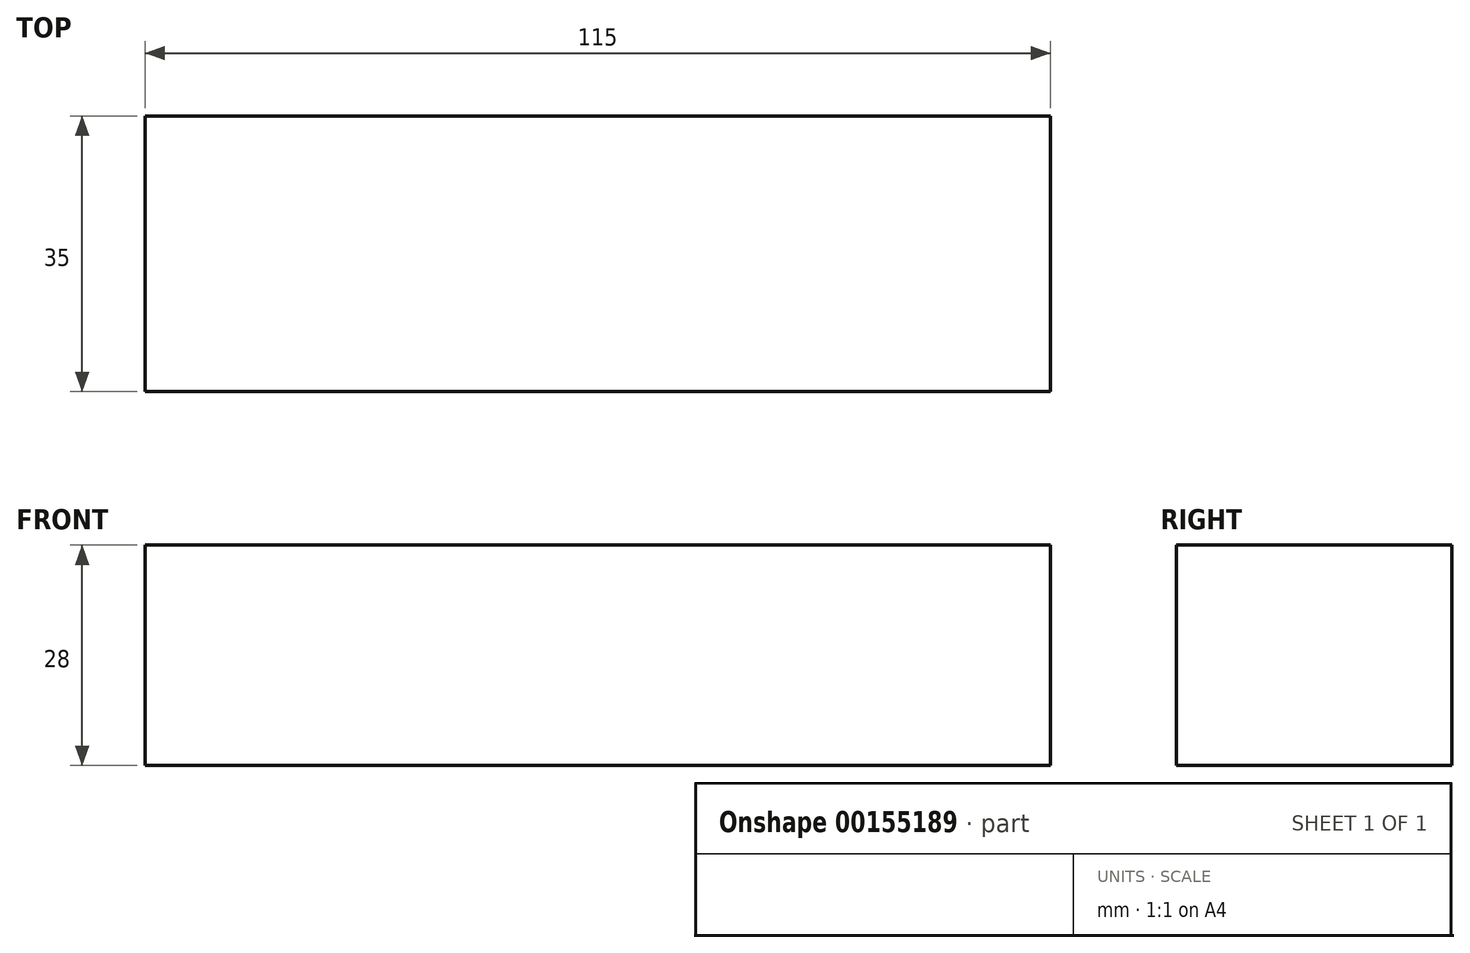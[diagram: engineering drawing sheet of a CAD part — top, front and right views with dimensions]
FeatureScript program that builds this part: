
annotation { "Feature Type Name" : "Feature", "Feature Type Description" : "" }
export const myFeature = defineFeature(function(context is Context, id is Id, definition is map)
    precondition{}
    {
        {
            var Q0;
            Q0=qCreatedBy(makeId("Top.planeOp"),FACE);
            var sketch = newSketch(context, id + "F0", { "sketchPlane" : qUnion([Q0])});
            skLineSegment(sketch, "E0.bottom", {"start": v(57.5, 17.5) * mm, "end": v(-57.5, 17.5) * mm});
            skLineSegment(sketch, "E0.top", {"start": v(57.5, -17.5) * mm, "end": v(-57.5, -17.5) * mm});
            skLineSegment(sketch, "E0.left", {"start": v(57.5, 17.5) * mm, "end": v(57.5, -17.5) * mm});
            skLineSegment(sketch, "E0.right", {"start": v(-57.5, 17.5) * mm, "end": v(-57.5, -17.5) * mm});
            skPoint(sketch, "E0.middle", {"position": v(0, 0) * mm});
            skSolve(sketch);
        }
        {
            var Q0;
            Q0=qSketchRegion(id+"F0",true);
            extrude(context, id + "F1", {"entities" : qUnion([Q0]), "endBound" : BoundingType.SYMMETRIC, "depth" : 28 * mm});
        }
    });
